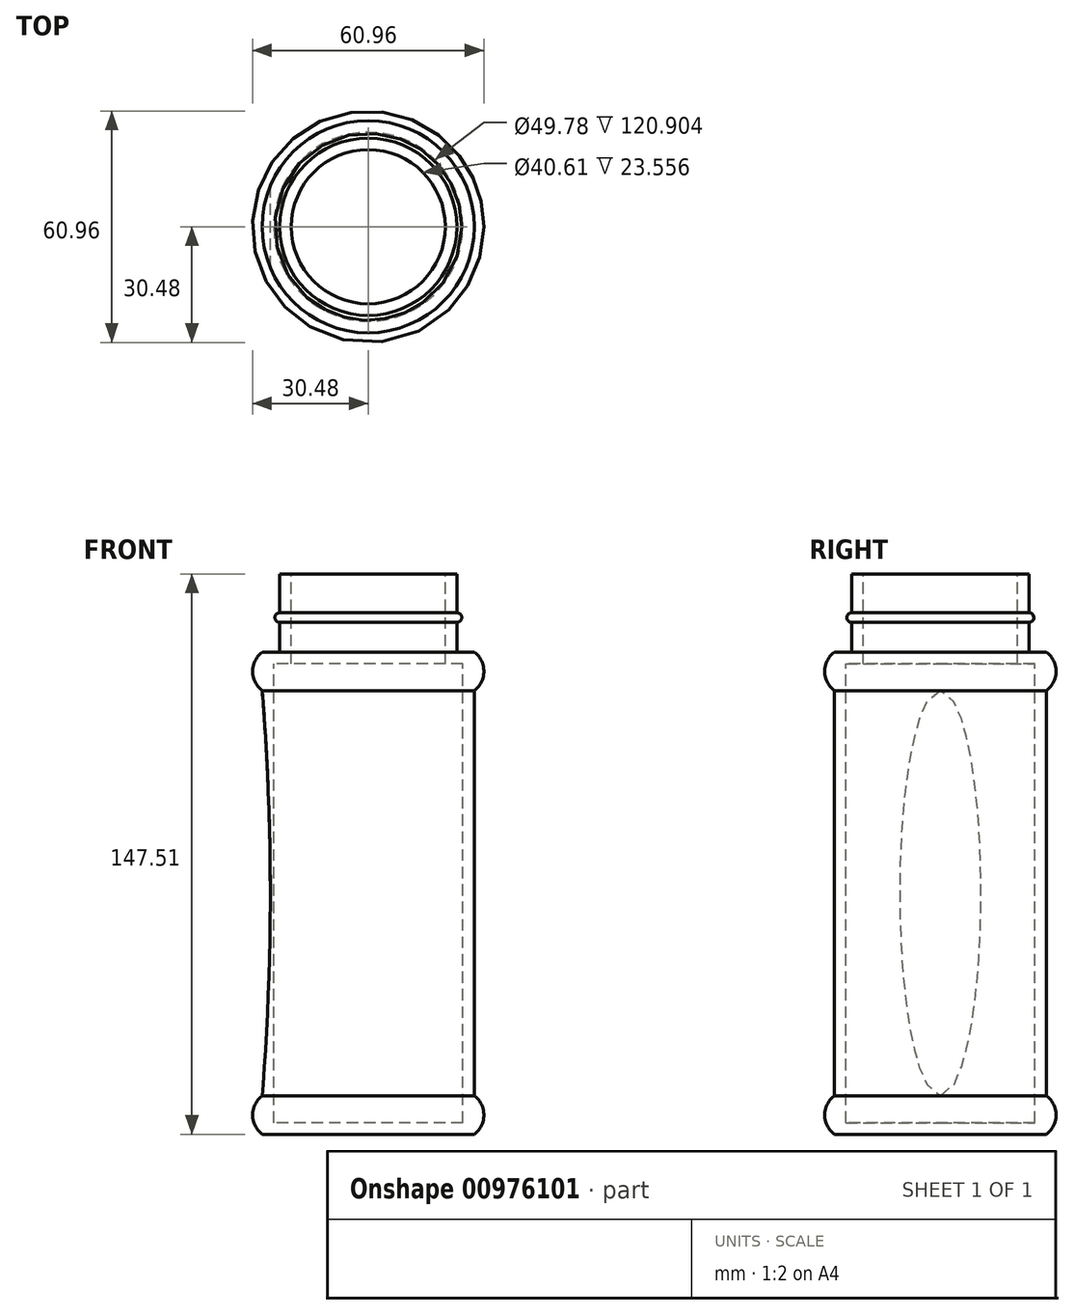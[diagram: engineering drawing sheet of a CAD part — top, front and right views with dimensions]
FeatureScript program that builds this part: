
annotation { "Feature Type Name" : "Feature", "Feature Type Description" : "" }
export const myFeature = defineFeature(function(context is Context, id is Id, definition is map)
    precondition{}
    {
        {
            var Q0;
            Q0=qCreatedBy(makeId("Front.planeOp"),FACE);
            var sketch = newSketch(context, id + "F0", { "sketchPlane" : qUnion([Q0])});
            skLineSegment(sketch, "E0.bottom", {"start": v(-27.94, 63.5) * mm, "end": v(-23.35, 63.5) * mm});
            skLineSegment(sketch, "E0.top", {"start": v(-27.94, -63.5) * mm, "end": v(0, -63.5) * mm});
            skLineSegment(sketch, "E1", {"start": v(-20.3, 84) * mm, "end": v(-23.35, 84) * mm});
            skLineSegment(sketch, "E2", {"start": v(-23.35, 84) * mm, "end": v(-23.35, 73.85) * mm});
            skLineSegment(sketch, "E3", {"start": v(-27.94, 53.34) * mm, "end": v(-27.94, -53.34) * mm});
            skArc(sketch, "E4", {"start": v(-27.94, 63.5) * mm, "mid": v(-30.48, 58.42) * mm, "end": v(-27.94, 53.34) * mm});
            skArc(sketch, "E5", {"start": v(-27.94, -53.34) * mm, "mid": v(-30.48, -58.42) * mm, "end": v(-27.94, -63.5) * mm});
            skArc(sketch, "E6", {"start": v(-23.35, 73.85) * mm, "mid": v(-24.62, 72.58) * mm, "end": v(-23.35, 71.3) * mm});
            skLineSegment(sketch, "E7.trimOffspring", {"start": v(-23.35, 71.3) * mm, "end": v(-23.35, 63.5) * mm});
            skLineSegment(sketch, "E8", {"start": v(0, 0) * mm, "end": v(0, 84) * mm});
            skLineSegment(sketch, "E9", {"start": v(0, 84) * mm, "end": v(0, -63.5) * mm});
            skPoint(sketch, "E10.start.orphan", {"position": v(27.94, -63.5) * mm});
            skPoint(sketch, "E11.start.orphan", {"position": v(27.94, -53.34) * mm});
            skPoint(sketch, "E12.start.orphan", {"position": v(27.94, 53.34) * mm});
            skPoint(sketch, "E13.orphan", {"position": v(27.94, 63.5) * mm});
            skLineSegment(sketch, "E14", {"start": v(-20.3, 84) * mm, "end": v(-20.3, 62.79) * mm});
            skLineSegment(sketch, "E15", {"start": v(-24.9, 54.11) * mm, "end": v(-24.9, -60.45) * mm});
            skLineSegment(sketch, "E16", {"start": v(-24.9, -60.45) * mm, "end": v(0, -60.45) * mm});
            skLineSegment(sketch, "E17", {"start": v(-20.3, 60.45) * mm, "end": v(-24.9, 60.45) * mm});
            skLineSegment(sketch, "E18", {"start": v(-24.9, 54.11) * mm, "end": v(-24.9, 60.45) * mm});
            skLineSegment(sketch, "E19", {"start": v(-20.3, 62.79) * mm, "end": v(-20.3, 60.45) * mm});
            skPoint(sketch, "E20.orphan", {"position": v(-26.77, 60.45) * mm});
            skSolve(sketch);
        }
        {
            var Q0;
            Q0=makeQuery(id+"F0.imprint","IMPRINT",FACE,{"disambiguationData":[TD([[makeQuery(id+"F0.imprint","IMPRINT",EDGE,{"derivedFrom":sQuery(id+"F0.wireOp",EDGE,"E0.bottom")}),-1.0]])]});
            var Q1;
            Q1=sQuery(id+"F0.wireOp",EDGE,"E9");
            revolve(context, id + "F1", {"surfaceOperationType" : NewSurfaceOperationType.NEW, "entities" : qUnion([Q0]), "axis" : qUnion([Q1]), "revolveType" : RevolveType.FULL});
        }
        {
            var Q0;
            Q0=qCreatedBy(makeId("Front.planeOp"),FACE);
            var sketch = newSketch(context, id + "F2", { "sketchPlane" : qUnion([Q0])});
            skLineSegment(sketch, "E21", {"start": v(-27.94, 53.34) * mm, "end": v(-30.74, 53.34) * mm});
            skLineSegment(sketch, "E22", {"start": v(-27.94, -53.34) * mm, "end": v(-31.3, -53.34) * mm});
            skArc(sketch, "E23", {"start": v(-27.94, -53.34) * mm, "mid": v(-25.81, 0) * mm, "end": v(-27.94, 53.34) * mm});
            skLineSegment(sketch, "E24", {"start": v(-30.74, 53.34) * mm, "end": v(-31.3, -53.34) * mm});
            skSolve(sketch);
        }
        {
            var Q0;
            Q0=makeQuery(id+"F2.imprint","IMPRINT",FACE,{"disambiguationData":[TD([[makeQuery(id+"F2.imprint","IMPRINT",EDGE,{"derivedFrom":sQuery(id+"F2.wireOp",EDGE,"E21")}),1.0]])]});
            extrude(context, id + "F3", {"entities" : qUnion([Q0]), "operationType" : NewBodyOperationType.REMOVE, "endBound" : BoundingType.SYMMETRIC, "depth" : 41.15 * mm, "offsetDistance" : 25.4 * mm});
        }
    });
